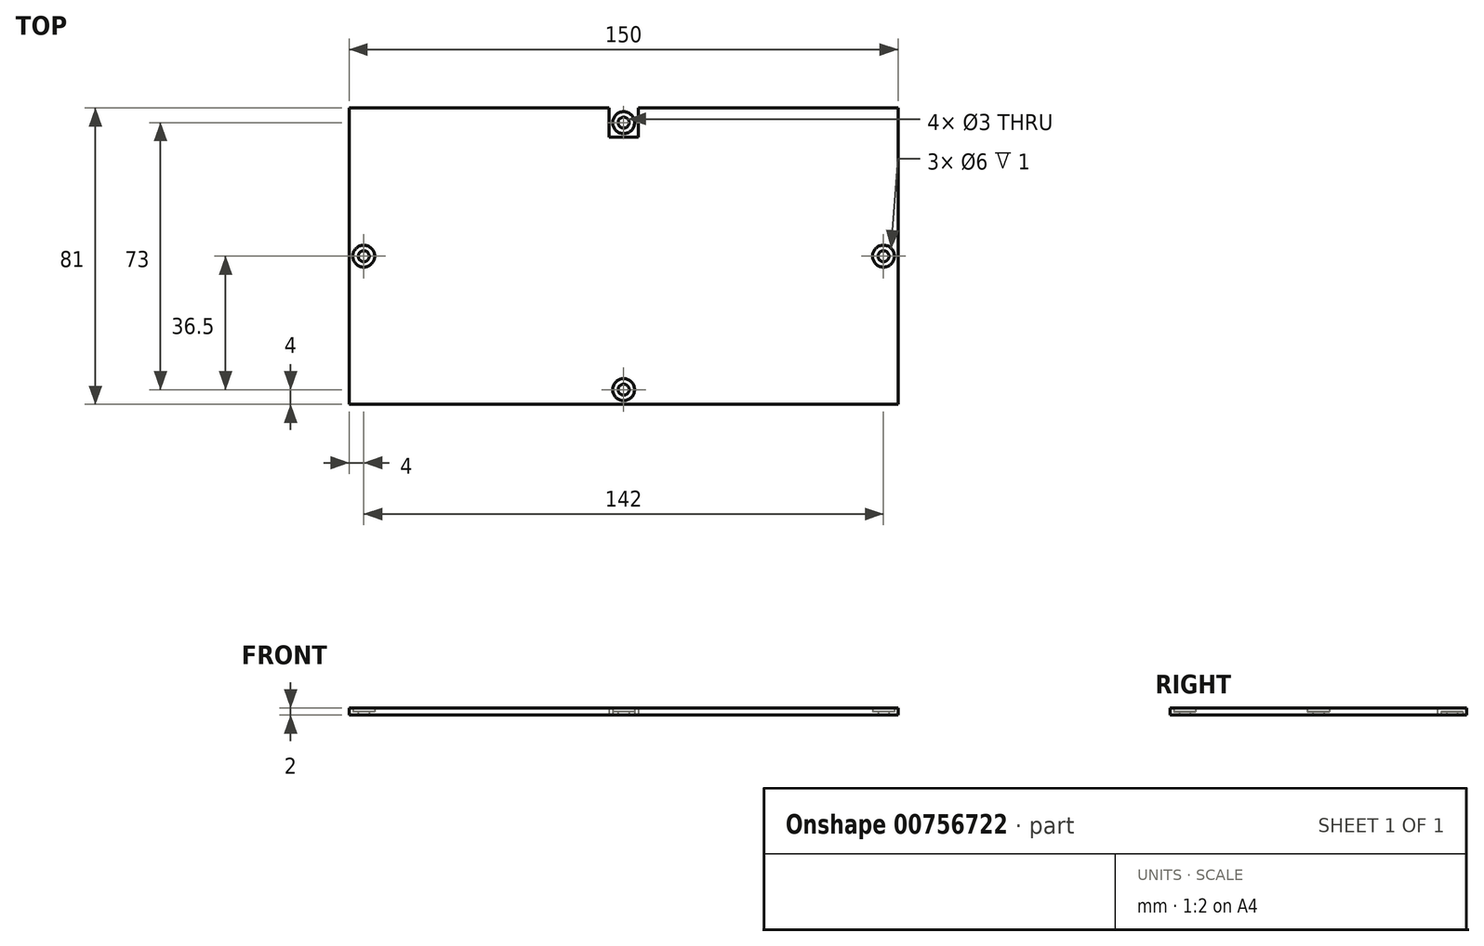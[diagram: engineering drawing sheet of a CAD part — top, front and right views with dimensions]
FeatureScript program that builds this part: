
annotation { "Feature Type Name" : "Feature", "Feature Type Description" : "" }
export const myFeature = defineFeature(function(context is Context, id is Id, definition is map)
    precondition{}
    {
        {
            var Q0;
            Q0=qCreatedBy(makeId("Top.planeOp"),FACE);
            var sketch = newSketch(context, id + "F0", { "sketchPlane" : qUnion([Q0])});
            skLineSegment(sketch, "E0.bottom", {"start": v(75, -40.5) * mm, "end": v(-75, -40.5) * mm});
            skLineSegment(sketch, "E0.top", {"start": v(75, 40.5) * mm, "end": v(-75, 40.5) * mm});
            skLineSegment(sketch, "E0.left", {"start": v(75, -40.5) * mm, "end": v(75, 40.5) * mm});
            skLineSegment(sketch, "E0.right", {"start": v(-75, -40.5) * mm, "end": v(-75, 40.5) * mm});
            skPoint(sketch, "E0.middle", {"position": v(0, 0) * mm});
            skLineSegment(sketch, "E1.bottom", {"start": v(-4, -32.5) * mm, "end": v(4, -32.5) * mm});
            skLineSegment(sketch, "E1.top", {"start": v(-4, -40.5) * mm, "end": v(4, -40.5) * mm});
            skLineSegment(sketch, "E1.left", {"start": v(-4, -32.5) * mm, "end": v(-4, -40.5) * mm});
            skLineSegment(sketch, "E1.right", {"start": v(4, -32.5) * mm, "end": v(4, -40.5) * mm});
            skLineSegment(sketch, "E2.bottom", {"start": v(75, 4) * mm, "end": v(67, 4) * mm});
            skLineSegment(sketch, "E2.top", {"start": v(75, -4) * mm, "end": v(67, -4) * mm});
            skLineSegment(sketch, "E2.left", {"start": v(75, 4) * mm, "end": v(75, -4) * mm});
            skLineSegment(sketch, "E2.right", {"start": v(67, 4) * mm, "end": v(67, -4) * mm});
            skLineSegment(sketch, "E3.bottom", {"start": v(-67, 4) * mm, "end": v(-75, 4) * mm});
            skLineSegment(sketch, "E3.top", {"start": v(-67, -4) * mm, "end": v(-75, -4) * mm});
            skLineSegment(sketch, "E3.left", {"start": v(-67, 4) * mm, "end": v(-67, -4) * mm});
            skLineSegment(sketch, "E3.right", {"start": v(-75, 4) * mm, "end": v(-75, -4) * mm});
            skLineSegment(sketch, "E4.bottom", {"start": v(4, 40.5) * mm, "end": v(-4, 40.5) * mm});
            skLineSegment(sketch, "E4.top", {"start": v(4, 32.5) * mm, "end": v(-4, 32.5) * mm});
            skLineSegment(sketch, "E4.left", {"start": v(4, 40.5) * mm, "end": v(4, 32.5) * mm});
            skLineSegment(sketch, "E4.right", {"start": v(-4, 40.5) * mm, "end": v(-4, 32.5) * mm});
            skPoint(sketch, "E5", {"position": v(-75, 0) * mm});
            skPoint(sketch, "E6", {"position": v(0, 40.5) * mm});
            skPoint(sketch, "E7", {"position": v(75, 0) * mm});
            skPoint(sketch, "E8", {"position": v(0, -40.5) * mm});
            skLineSegment(sketch, "E9", {"start": v(-67, 4) * mm, "end": v(-75, -4) * mm, "construction": true});
            skLineSegment(sketch, "E10", {"start": v(4, 32.5) * mm, "end": v(-4, 40.5) * mm, "construction": true});
            skLineSegment(sketch, "E11", {"start": v(-4, -40.5) * mm, "end": v(4, -32.5) * mm, "construction": true});
            skLineSegment(sketch, "E12", {"start": v(67, 4) * mm, "end": v(75, -4) * mm, "construction": true});
            skCircle(sketch, "E13", {"center": v(0, 36.5) * mm, "radius": 1.5 * mm});
            skCircle(sketch, "E14", {"center": v(-71, 0) * mm, "radius": 1.5 * mm});
            skCircle(sketch, "E15", {"center": v(0, -36.5) * mm, "radius": 1.5 * mm});
            skCircle(sketch, "E16", {"center": v(71, 0) * mm, "radius": 1.5 * mm});
            skCircle(sketch, "E17", {"center": v(-71, 0) * mm, "radius": 3 * mm});
            skCircle(sketch, "E18", {"center": v(0, 36.5) * mm, "radius": 3 * mm});
            skCircle(sketch, "E19", {"center": v(0, -36.5) * mm, "radius": 3 * mm});
            skCircle(sketch, "E20", {"center": v(71, 0) * mm, "radius": 3 * mm});
            skSolve(sketch);
        }
        {
            var Q0;
            Q0=makeQuery(id+"F0.imprint","IMPRINT",FACE,{"disambiguationData":[TD([[makeQuery(id+"F0.imprint","IMPRINT",EDGE,{"derivedFrom":sQuery(id+"F0.wireOp",EDGE,"E0.bottom")}),-1.0]])]});
            var Q1;
            Q1=makeQuery(id+"F0.imprint","IMPRINT",FACE,{"disambiguationData":[TD([[makeQuery(id+"F0.imprint","IMPRINT",EDGE,{"derivedFrom":sQuery(id+"F0.wireOp",EDGE,"2VD1PUbU-qxal-EaX9-lvTG-zuy5S37opT7H.bottom")}),-1.0]])]});
            var Q2;
            Q2=makeQuery(id+"F0.imprint","IMPRINT",FACE,{"disambiguationData":[TD([[makeQuery(id+"F0.imprint","IMPRINT",EDGE,{"derivedFrom":sQuery(id+"F0.wireOp",EDGE,"cEnfu8JC-ueyC-NaVJ-b6WP-igvS2lgiipei.bottom")}),1.0]])]});
            var Q3;
            Q3=makeQuery(id+"F0.imprint","IMPRINT",FACE,{"disambiguationData":[TD([[makeQuery(id+"F0.imprint","IMPRINT",EDGE,{"derivedFrom":sQuery(id+"F0.wireOp",EDGE,"FASCe2rB-3TVz-9DCP-6yKu-A9yiWA1enJAh.bottom")}),-1.0]])]});
            var Q4;
            Q4=makeQuery(id+"F0.imprint","IMPRINT",FACE,{"disambiguationData":[TD([[makeQuery(id+"F0.imprint","IMPRINT",EDGE,{"derivedFrom":sQuery(id+"F0.wireOp",EDGE,"GTzzIUKF-CErc-WRk4-LmGR-4SaPmRghxuXT.bottom")}),1.0]])]});
            var Q5;
            Q5=makeQuery(id+"F0.imprint","IMPRINT",FACE,{"disambiguationData":[TD([[makeQuery(id+"F0.imprint","IMPRINT",EDGE,{"derivedFrom":sQuery(id+"F0.wireOp",EDGE,"E3.bottom")}),1.0]])]});
            var Q6;
            Q6=makeQuery(id+"F0.imprint","IMPRINT",FACE,{"disambiguationData":[TD([[makeQuery(id+"F0.imprint","IMPRINT",EDGE,{"derivedFrom":sQuery(id+"F0.wireOp",EDGE,"E4.bottom")}),1.0]])]});
            var Q7;
            Q7=makeQuery(id+"F0.imprint","IMPRINT",FACE,{"disambiguationData":[TD([[makeQuery(id+"F0.imprint","IMPRINT",EDGE,{"derivedFrom":sQuery(id+"F0.wireOp",EDGE,"E2.bottom")}),1.0]])]});
            var Q8;
            Q8=makeQuery(id+"F0.imprint","IMPRINT",FACE,{"disambiguationData":[TD([[makeQuery(id+"F0.imprint","IMPRINT",EDGE,{"derivedFrom":sQuery(id+"F0.wireOp",EDGE,"E1.bottom")}),-1.0]])]});
            extrude(context, id + "F1", {"entities" : qUnion([Q0, Q1, Q2, Q3, Q4, Q5, Q6, Q7, Q8]), "depth" : 2 * mm, "offsetDistance" : 25 * mm});
        }
        {
            var Q0;
            Q0=makeQuery(id+"F0.imprint","IMPRINT",FACE,{"disambiguationData":[TD([[makeQuery(id+"F0.imprint","IMPRINT",EDGE,{"derivedFrom":sQuery(id+"F0.wireOp",EDGE,"E13")}),-1.0]])]});
            var Q1;
            Q1=makeQuery(id+"F0.imprint","IMPRINT",FACE,{"disambiguationData":[TD([[makeQuery(id+"F0.imprint","IMPRINT",EDGE,{"derivedFrom":sQuery(id+"F0.wireOp",EDGE,"E16")}),-1.0]])]});
            var Q2;
            Q2=makeQuery(id+"F0.imprint","IMPRINT",FACE,{"disambiguationData":[TD([[makeQuery(id+"F0.imprint","IMPRINT",EDGE,{"derivedFrom":sQuery(id+"F0.wireOp",EDGE,"E15")}),-1.0]])]});
            var Q3;
            Q3=makeQuery(id+"F0.imprint","IMPRINT",FACE,{"disambiguationData":[TD([[makeQuery(id+"F0.imprint","IMPRINT",EDGE,{"derivedFrom":sQuery(id+"F0.wireOp",EDGE,"E14")}),-1.0]])]});
            extrude(context, id + "F2", {"entities" : qUnion([Q0, Q1, Q2, Q3]), "operationType" : NewBodyOperationType.ADD, "depth" : 1 * mm, "offsetDistance" : 25 * mm});
        }
    });
